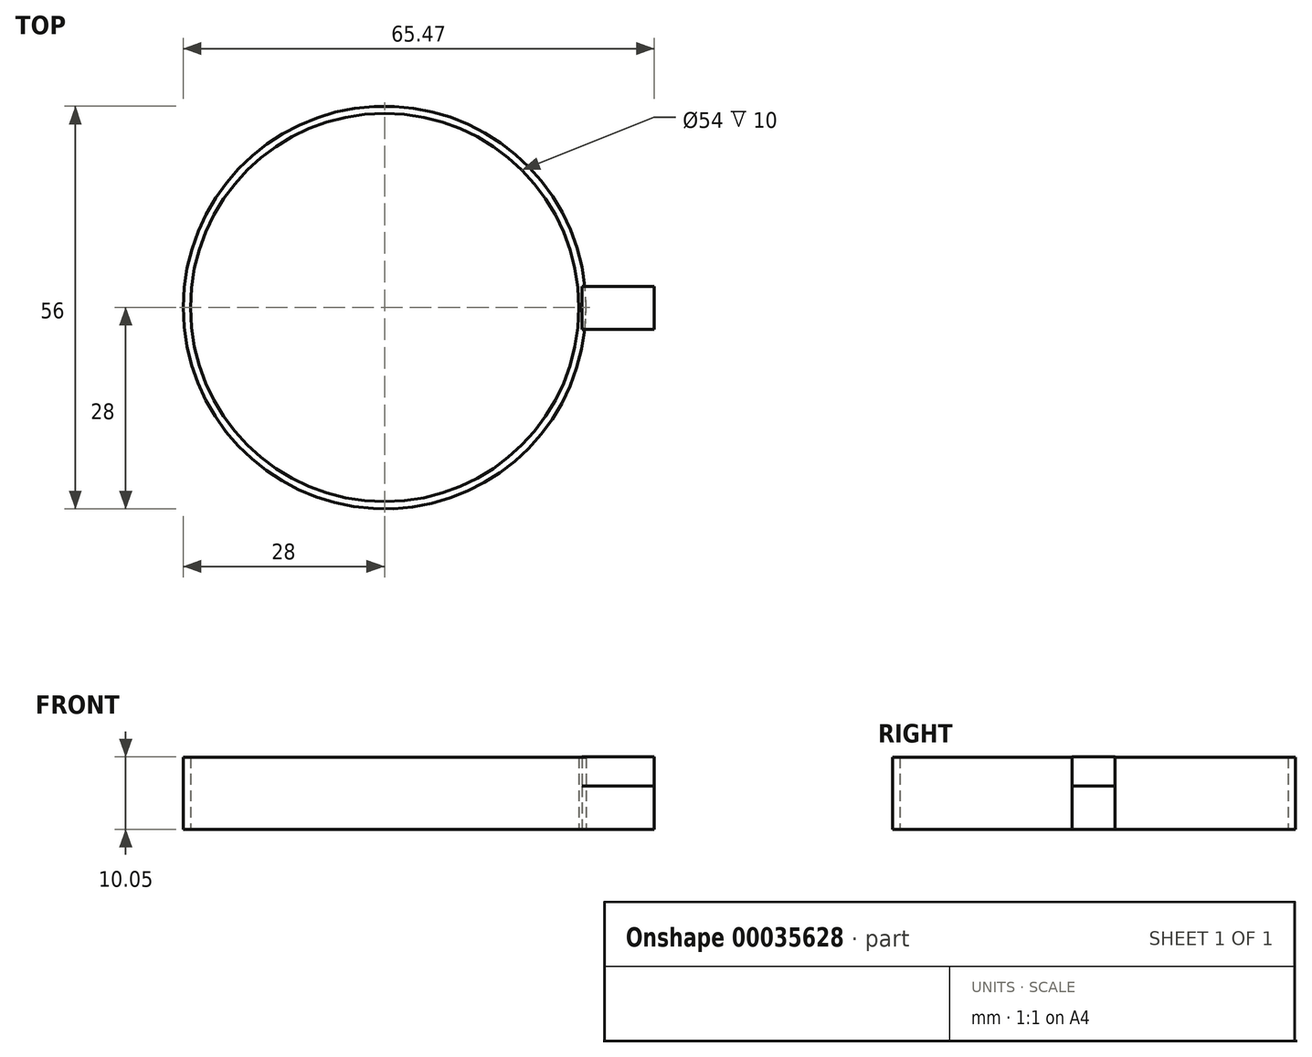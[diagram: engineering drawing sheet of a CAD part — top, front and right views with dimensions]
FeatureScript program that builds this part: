
annotation { "Feature Type Name" : "Feature", "Feature Type Description" : "" }
export const myFeature = defineFeature(function(context is Context, id is Id, definition is map)
    precondition{}
    {
        {
            var Q0;
            Q0=qCreatedBy(makeId("Top.planeOp"),FACE);
            var sketch = newSketch(context, id + "F0", { "sketchPlane" : qUnion([Q0])});
            skCircle(sketch, "E0", {"center": v(0, 0) * mm, "radius": 28 * mm});
            skSolve(sketch);
        }
        {
            var Q0;
            Q0=qCreatedBy(makeId("Top.planeOp"),FACE);
            var sketch = newSketch(context, id + "F1", { "sketchPlane" : qUnion([Q0])});
            skCircle(sketch, "E1", {"center": v(0, 0) * mm, "radius": 27 * mm});
            skSolve(sketch);
        }
        {
            var Q0;
            Q0=makeQuery(id+"F1.imprint","IMPRINT",FACE,{"disambiguationData":[TD([[makeQuery(id+"F1.imprint","IMPRINT",EDGE,{"derivedFrom":sQuery(id+"F1.wireOp",EDGE,"E1")}),1.0]])]});
            var Q1;
            Q1=sQuery(id+"F1.wireOp",EDGE,"E1");
            extrude(context, id + "F2", {"entities" : qUnion([Q0]), "surfaceEntities" : qUnion([Q1]), "depth" : 30 * mm});
        }
        {
            var Q0;
            Q0=makeQuery(id+"F0.imprint","IMPRINT",FACE,{"disambiguationData":[TD([[makeQuery(id+"F0.imprint","IMPRINT",EDGE,{"derivedFrom":sQuery(id+"F0.wireOp",EDGE,"E0")}),1.0]])]});
            extrude(context, id + "F3", {"entities" : qUnion([Q0]), "depth" : 10 * mm});
        }
        {
            var Q0;
            Q0=makeQuery(id+"F2.opExtrude","SWEPT_BODY",BODY,{"disambiguationData":[OSD([sQuery(id+"F1.wireOp",EDGE,"E1")])]});
            var Q1;
            Q1=makeQuery(id+"F3.opExtrude","SWEPT_BODY",BODY,{"disambiguationData":[OSD([sQuery(id+"F0.wireOp",EDGE,"E0")])]});
            booleanBodies(context, id + "F4", {"operationType" : BooleanOperationType.SUBTRACTION, "tools" : qUnion([Q0]), "targets" : qUnion([Q1])});
        }
        {
            var Q0;
            Q0=qCreatedBy(makeId("Top.planeOp"),FACE);
            var sketch = newSketch(context, id + "F5", { "sketchPlane" : qUnion([Q0])});
            skLineSegment(sketch, "E2.bottom", {"start": v(27.47, -3.06) * mm, "end": v(37.47, -3.06) * mm});
            skLineSegment(sketch, "E2.top", {"start": v(27.47, 2.94) * mm, "end": v(37.47, 2.94) * mm});
            skLineSegment(sketch, "E2.left", {"start": v(27.47, -3.06) * mm, "end": v(27.47, 2.94) * mm});
            skLineSegment(sketch, "E2.right", {"start": v(37.47, -3.06) * mm, "end": v(37.47, 2.94) * mm});
            skSolve(sketch);
        }
        {
            var Q0;
            Q0=makeQuery(id+"F5.imprint","IMPRINT",FACE,{"disambiguationData":[TD([[makeQuery(id+"F5.imprint","IMPRINT",EDGE,{"derivedFrom":sQuery(id+"F5.wireOp",EDGE,"E2.bottom")}),1.0]])]});
            extrude(context, id + "F6", {"entities" : qUnion([Q0]), "depth" : 6 * mm});
        }
        {
            var Q0;
            Q0=makeQuery(id+"F6.opExtrude","CAP_FACE",FACE,{"disambiguationData":[OSD([sQuery(id+"F5.wireOp",EDGE,"E2.bottom"),sQuery(id+"F5.wireOp",EDGE,"E2.top"),sQuery(id+"F5.wireOp",EDGE,"E2.left"),sQuery(id+"F5.wireOp",EDGE,"E2.right")])],"isStart":false});
            extrude(context, id + "F7", {"entities" : qUnion([Q0]), "depth" : 4.05 * mm});
        }
    });
